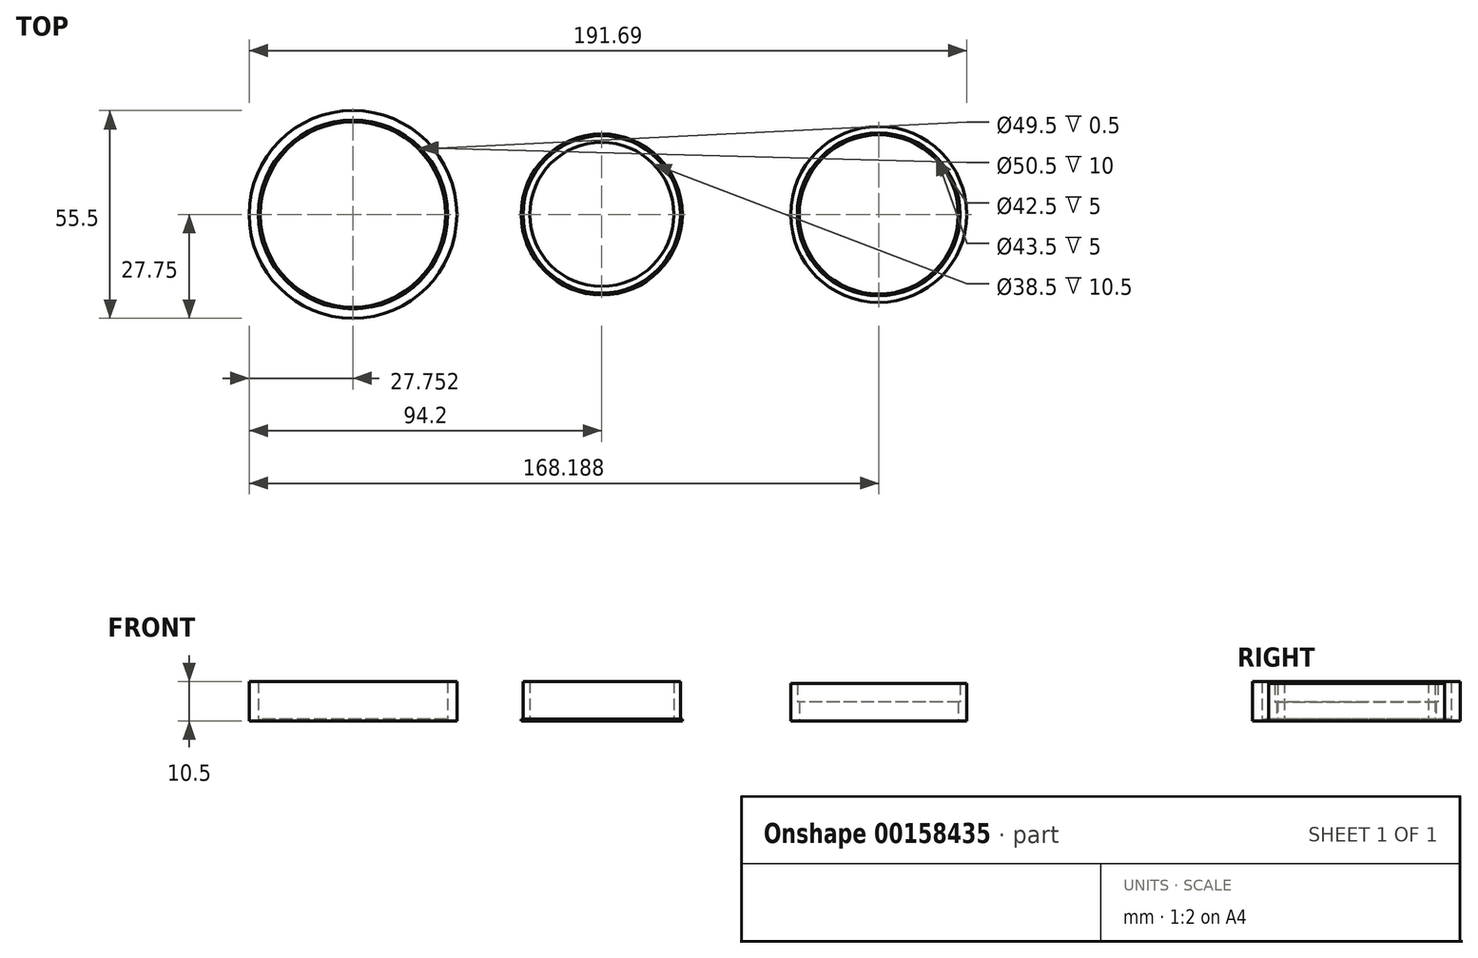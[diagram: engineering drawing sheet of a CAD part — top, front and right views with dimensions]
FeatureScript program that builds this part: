
annotation { "Feature Type Name" : "Feature", "Feature Type Description" : "" }
export const myFeature = defineFeature(function(context is Context, id is Id, definition is map)
    precondition{}
    {
        {
            var Q0;
            Q0=qCreatedBy(makeId("Top.planeOp"),FACE);
            var sketch = newSketch(context, id + "F0", { "sketchPlane" : qUnion([Q0])});
            skCircle(sketch, "E0", {"center": v(0, 0) * mm, "radius": 19.25 * mm});
            skCircle(sketch, "E1", {"center": v(0, 0) * mm, "radius": 21.5 * mm});
            skSolve(sketch);
        }
        {
            var Q0;
            Q0=makeQuery(id+"F0.imprint","IMPRINT",FACE,{"disambiguationData":[TD([[makeQuery(id+"F0.imprint","IMPRINT",EDGE,{"derivedFrom":sQuery(id+"F0.wireOp",EDGE,"E0")}),-1.0]])]});
            extrude(context, id + "F1", {"entities" : qUnion([Q0]), "depth" : 0.5 * mm});
        }
        {
            var Q0;
            Q0=makeQuery(id+"F1.opExtrude","CAP_FACE",FACE,{"disambiguationData":[OSD([sQuery(id+"F0.wireOp",EDGE,"E0"),sQuery(id+"F0.wireOp",EDGE,"E1")])],"isStart":false});
            var sketch = newSketch(context, id + "F2", { "sketchPlane" : qUnion([Q0])});
            skCircle(sketch, "E2", {"center": v(0, 0) * mm, "radius": 19.25 * mm});
            skCircle(sketch, "E3", {"center": v(0, 0) * mm, "radius": 21 * mm});
            skSolve(sketch);
        }
        {
            var Q0;
            Q0=makeQuery(id+"F2.imprint","IMPRINT",FACE,{"disambiguationData":[TD([[makeQuery(id+"F2.imprint","IMPRINT",EDGE,{"derivedFrom":sQuery(id+"F2.wireOp",EDGE,"E2")}),-1.0]])]});
            extrude(context, id + "F3", {"entities" : qUnion([Q0]), "operationType" : NewBodyOperationType.ADD, "depth" : 10 * mm});
        }
        {
            var Q0;
            Q0=qCreatedBy(makeId("Top.planeOp"),FACE);
            var sketch = newSketch(context, id + "F4", { "sketchPlane" : qUnion([Q0])});
            skCircle(sketch, "E4", {"center": v(73.99, 0) * mm, "radius": 21.25 * mm});
            skCircle(sketch, "E5", {"center": v(73.99, 0) * mm, "radius": 23.5 * mm});
            skSolve(sketch);
        }
        {
            var Q0;
            Q0=makeQuery(id+"F4.imprint","IMPRINT",FACE,{"disambiguationData":[TD([[makeQuery(id+"F4.imprint","IMPRINT",EDGE,{"derivedFrom":sQuery(id+"F4.wireOp",EDGE,"E4")}),-1.0]])]});
            extrude(context, id + "F5", {"entities" : qUnion([Q0]), "depth" : 5 * mm});
        }
        {
            var Q0;
            Q0=makeQuery(id+"F5.opExtrude","CAP_FACE",FACE,{"disambiguationData":[OSD([sQuery(id+"F4.wireOp",EDGE,"E4"),sQuery(id+"F4.wireOp",EDGE,"E5")])],"isStart":false});
            var sketch = newSketch(context, id + "F6", { "sketchPlane" : qUnion([Q0])});
            skCircle(sketch, "E6", {"center": v(73.99, 0) * mm, "radius": 23.5 * mm});
            skCircle(sketch, "E7", {"center": v(73.99, 0) * mm, "radius": 21.75 * mm});
            skSolve(sketch);
        }
        {
            var Q0;
            Q0=makeQuery(id+"F6.imprint","IMPRINT",FACE,{"disambiguationData":[TD([[makeQuery(id+"F6.imprint","IMPRINT",EDGE,{"derivedFrom":sQuery(id+"F6.wireOp",EDGE,"E6")}),1.0]])]});
            extrude(context, id + "F7", {"entities" : qUnion([Q0]), "operationType" : NewBodyOperationType.ADD, "depth" : 5 * mm});
        }
        {
            var Q0;
            Q0=qCreatedBy(makeId("Top.planeOp"),FACE);
            var sketch = newSketch(context, id + "F8", { "sketchPlane" : qUnion([Q0])});
            skCircle(sketch, "E8", {"center": v(-66.45, 0) * mm, "radius": 24.75 * mm});
            skCircle(sketch, "E9", {"center": v(-66.45, 0) * mm, "radius": 27.75 * mm});
            skSolve(sketch);
        }
        {
            var Q0;
            Q0=makeQuery(id+"F8.imprint","IMPRINT",FACE,{"disambiguationData":[TD([[makeQuery(id+"F8.imprint","IMPRINT",EDGE,{"derivedFrom":sQuery(id+"F8.wireOp",EDGE,"E8")}),-1.0]])]});
            extrude(context, id + "F9", {"entities" : qUnion([Q0]), "depth" : 0.5 * mm});
        }
        {
            var Q0;
            Q0=makeQuery(id+"F9.opExtrude","CAP_FACE",FACE,{"disambiguationData":[OSD([sQuery(id+"F8.wireOp",EDGE,"E8"),sQuery(id+"F8.wireOp",EDGE,"E9")])],"isStart":false});
            var sketch = newSketch(context, id + "F10", { "sketchPlane" : qUnion([Q0])});
            skCircle(sketch, "E10", {"center": v(-66.45, 0) * mm, "radius": 27.75 * mm});
            skCircle(sketch, "E11", {"center": v(-66.45, 0) * mm, "radius": 25.25 * mm});
            skSolve(sketch);
        }
        {
            var Q0;
            Q0=makeQuery(id+"F10.imprint","IMPRINT",FACE,{"disambiguationData":[TD([[makeQuery(id+"F10.imprint","IMPRINT",EDGE,{"derivedFrom":sQuery(id+"F10.wireOp",EDGE,"E10")}),1.0]])]});
            extrude(context, id + "F11", {"entities" : qUnion([Q0]), "operationType" : NewBodyOperationType.ADD, "depth" : 10 * mm});
        }
    });
